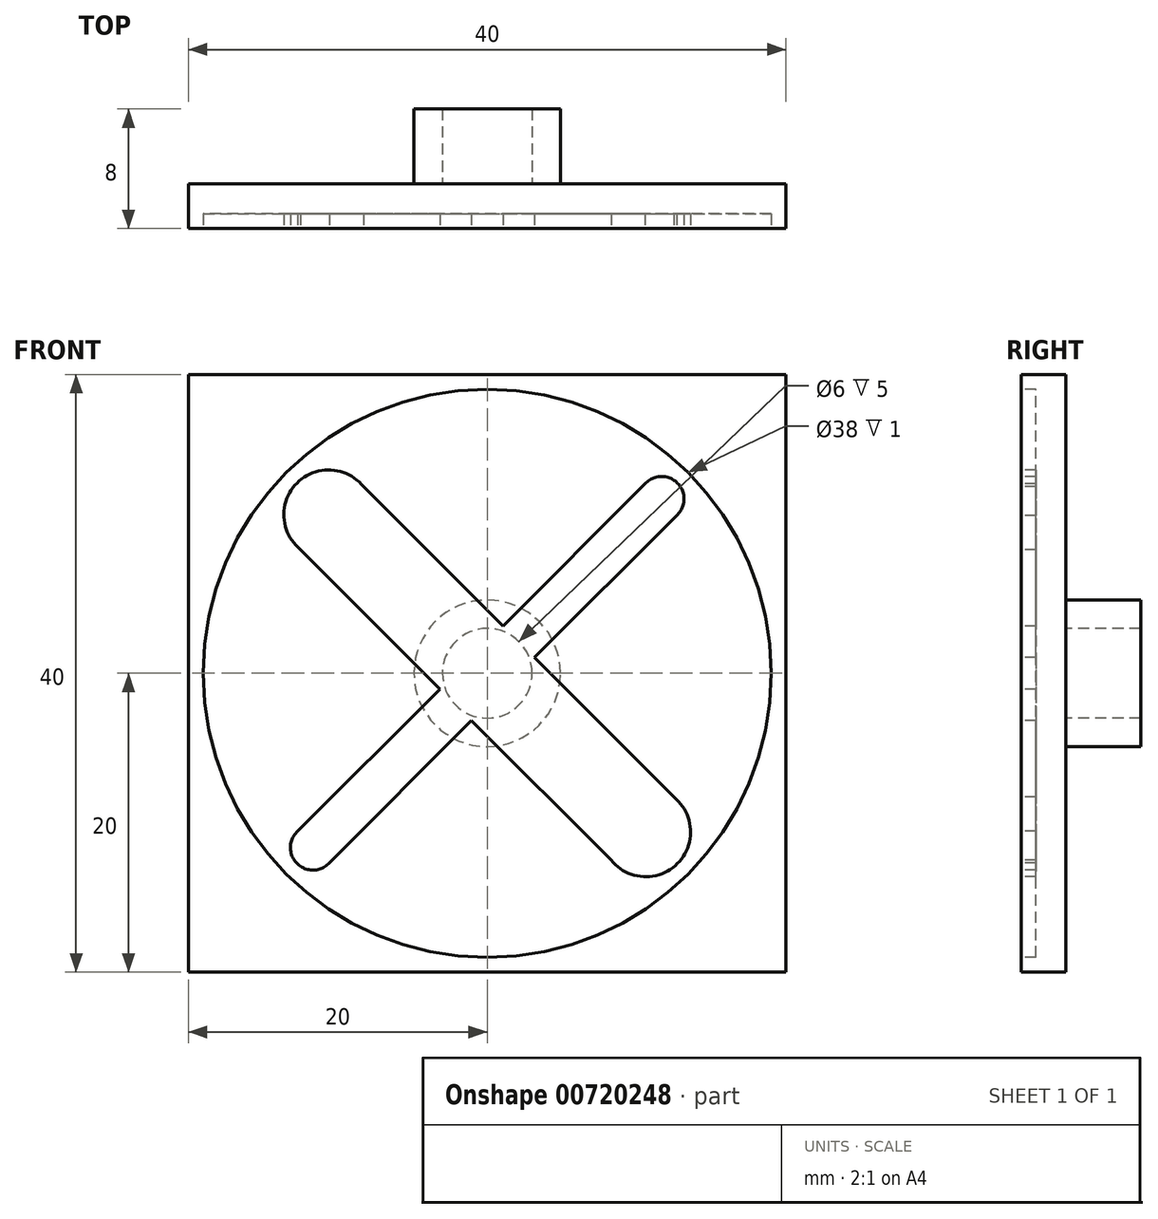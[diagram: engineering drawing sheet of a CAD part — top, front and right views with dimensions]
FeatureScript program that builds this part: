
annotation { "Feature Type Name" : "Feature", "Feature Type Description" : "" }
export const myFeature = defineFeature(function(context is Context, id is Id, definition is map)
    precondition{}
    {
        {
            var Q0;
            Q0=qCreatedBy(makeId("Front.planeOp"),FACE);
            var sketch = newSketch(context, id + "F0", { "sketchPlane" : qUnion([Q0])});
            skLineSegment(sketch, "E0.bottom", {"start": v(20, 20) * mm, "end": v(-20, 20) * mm});
            skLineSegment(sketch, "E0.top", {"start": v(20, -20) * mm, "end": v(-20, -20) * mm});
            skLineSegment(sketch, "E0.left", {"start": v(20, 20) * mm, "end": v(20, -20) * mm});
            skLineSegment(sketch, "E0.right", {"start": v(-20, 20) * mm, "end": v(-20, -20) * mm});
            skPoint(sketch, "E0.middle", {"position": v(0, 0) * mm});
            skSolve(sketch);
        }
        {
            var Q0;
            Q0=makeQuery(id+"F0.imprint","IMPRINT",FACE,{"disambiguationData":[TD([[makeQuery(id+"F0.imprint","IMPRINT",EDGE,{"derivedFrom":sQuery(id+"F0.wireOp",EDGE,"E0.bottom")}),1.0]])]});
            extrude(context, id + "F1", {"entities" : qUnion([Q0]), "depth" : 3 * mm, "offsetDistance" : 25 * mm});
        }
        {
            var Q0;
            Q0=makeQuery(id+"F1.opExtrude","CAP_FACE",FACE,{"disambiguationData":[OSD([sQuery(id+"F0.wireOp",EDGE,"E0.bottom"),sQuery(id+"F0.wireOp",EDGE,"E0.top"),sQuery(id+"F0.wireOp",EDGE,"E0.left"),sQuery(id+"F0.wireOp",EDGE,"E0.right")])],"isStart":true});
            var sketch = newSketch(context, id + "F2", { "sketchPlane" : qUnion([Q0])});
            skCircle(sketch, "E1", {"center": v(0, 0) * mm, "radius": 4.9 * mm});
            skCircle(sketch, "E2", {"center": v(0, 0) * mm, "radius": 3 * mm});
            skSolve(sketch);
        }
        {
            var Q0;
            Q0=makeQuery(id+"F2.imprint","IMPRINT",FACE,{"disambiguationData":[TD([[makeQuery(id+"F2.imprint","IMPRINT",EDGE,{"derivedFrom":sQuery(id+"F2.wireOp",EDGE,"E1")}),1.0]])]});
            extrude(context, id + "F3", {"entities" : qUnion([Q0]), "operationType" : NewBodyOperationType.ADD, "depth" : 5 * mm, "offsetDistance" : 25 * mm});
        }
        {
            var Q0;
            Q0=makeQuery(id+"F1.opExtrude","CAP_FACE",FACE,{"disambiguationData":[OSD([sQuery(id+"F0.wireOp",EDGE,"E0.bottom"),sQuery(id+"F0.wireOp",EDGE,"E0.top"),sQuery(id+"F0.wireOp",EDGE,"E0.left"),sQuery(id+"F0.wireOp",EDGE,"E0.right")])],"isStart":false});
            var sketch = newSketch(context, id + "F4", { "sketchPlane" : qUnion([Q0])});
            skCircle(sketch, "E3", {"center": v(0, 0) * mm, "radius": 19 * mm});
            skArc(sketch, "E4", {"start": v(-8.28, 12.5) * mm, "mid": v(-12.73, 12.73) * mm, "end": v(-12.5, 8.28) * mm});
            skArc(sketch, "E5", {"start": v(8.28, -12.5) * mm, "mid": v(12.73, -12.73) * mm, "end": v(12.5, -8.28) * mm});
            skArc(sketch, "E6", {"start": v(12.68, 10.56) * mm, "mid": v(12.73, 12.73) * mm, "end": v(10.56, 12.68) * mm});
            skArc(sketch, "E7", {"start": v(-12.68, -10.56) * mm, "mid": v(-12.73, -12.73) * mm, "end": v(-10.56, -12.68) * mm});
            skLineSegment(sketch, "E8", {"start": v(-12.5, 8.28) * mm, "end": v(8.28, -12.5) * mm});
            skLineSegment(sketch, "E9", {"start": v(-8.28, 12.5) * mm, "end": v(12.5, -8.28) * mm});
            skLineSegment(sketch, "E10", {"start": v(10.56, 12.68) * mm, "end": v(-12.68, -10.56) * mm});
            skLineSegment(sketch, "E11", {"start": v(-10.56, -12.68) * mm, "end": v(12.68, 10.56) * mm});
            skSolve(sketch);
        }
        {
            var Q0;
            Q0=makeQuery(id+"F4.imprint","IMPRINT",FACE,{"disambiguationData":[TD([[makeQuery(id+"F4.imprint","IMPRINT",EDGE,{"derivedFrom":sQuery(id+"F4.wireOp",EDGE,"E3")}),1.0]])]});
            extrude(context, id + "F5", {"entities" : qUnion([Q0]), "operationType" : NewBodyOperationType.REMOVE, "oppositeDirection" : true, "depth" : 1 * mm, "offsetDistance" : 25 * mm});
        }
    });
